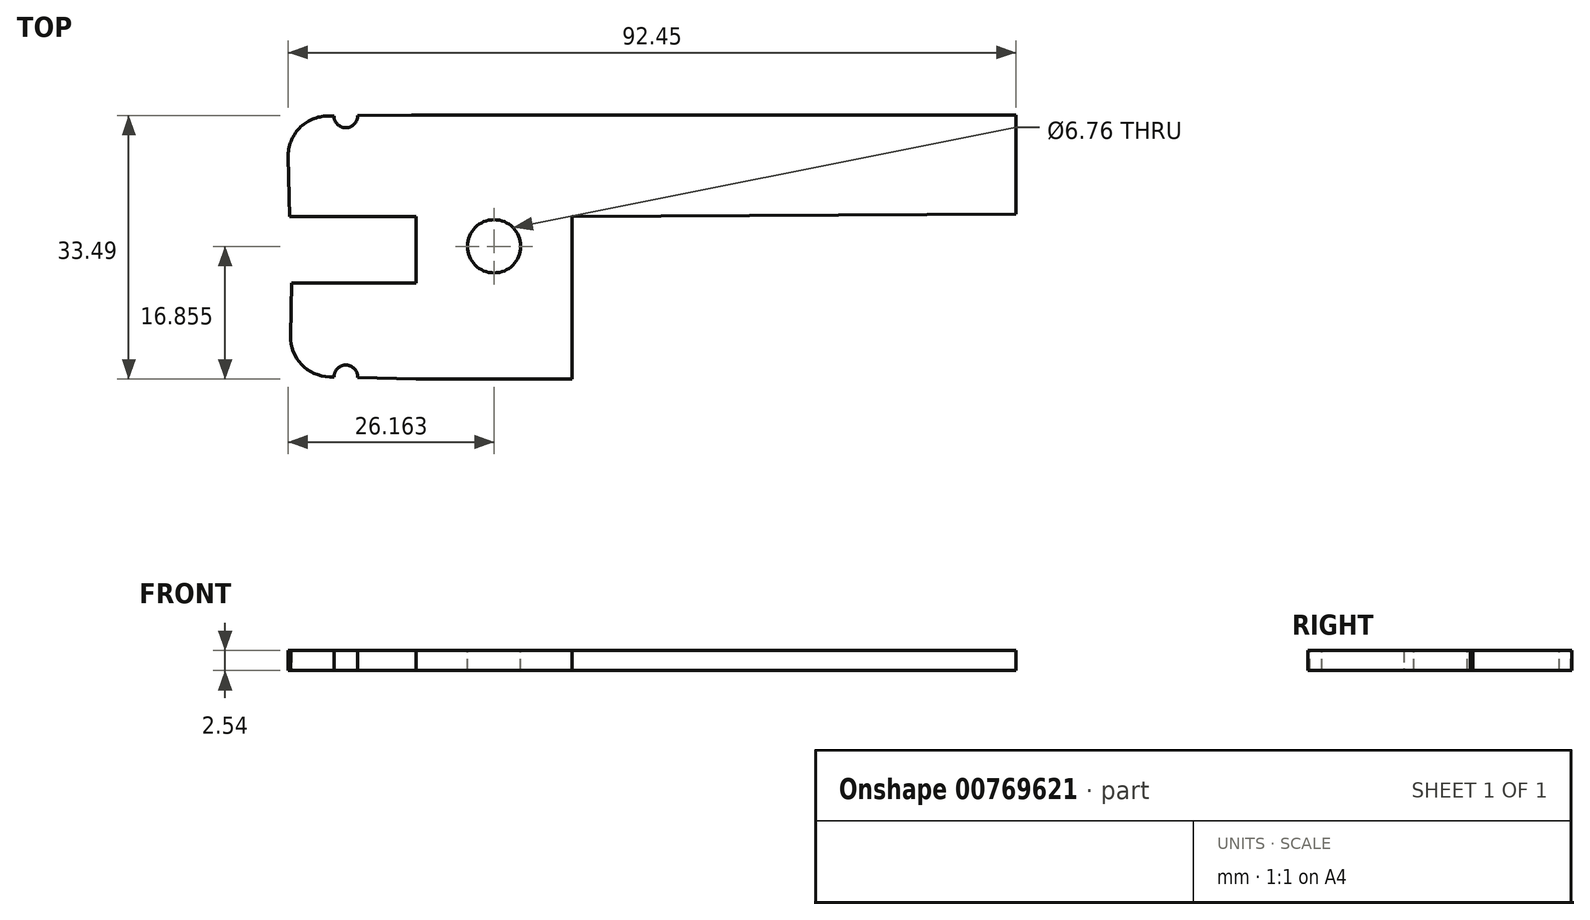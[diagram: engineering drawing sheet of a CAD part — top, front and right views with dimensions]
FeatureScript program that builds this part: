
annotation { "Feature Type Name" : "Feature", "Feature Type Description" : "" }
export const myFeature = defineFeature(function(context is Context, id is Id, definition is map)
    precondition{}
    {
        {
            var Q0;
            Q0=qCreatedBy(makeId("Top.planeOp"),FACE);
            var sketch = newSketch(context, id + "F0", { "sketchPlane" : qUnion([Q0])});
            skLineSegment(sketch, "E0", {"start": v(-46, 24.97) * mm, "end": v(-29.94, 24.97) * mm});
            skLineSegment(sketch, "E1", {"start": v(-29.94, 24.97) * mm, "end": v(-29.94, 16.5) * mm});
            skLineSegment(sketch, "E2", {"start": v(-29.94, 16.5) * mm, "end": v(-45.7, 16.5) * mm});
            skLineSegment(sketch, "E3", {"start": v(-45.7, 16.5) * mm, "end": v(-46, 4.72) * mm});
            skLineSegment(sketch, "E4", {"start": v(-46, 4.72) * mm, "end": v(-29.94, 4.32) * mm});
            skLineSegment(sketch, "E5", {"start": v(-29.94, 4.32) * mm, "end": v(-10.08, 4.32) * mm});
            skLineSegment(sketch, "E6", {"start": v(-10.08, 4.32) * mm, "end": v(-10.08, 24.97) * mm});
            skLineSegment(sketch, "E7", {"start": v(-46.3, 37.68) * mm, "end": v(-46, 24.97) * mm});
            skLineSegment(sketch, "E8", {"start": v(-46.3, 37.68) * mm, "end": v(-30.51, 37.81) * mm});
            skLineSegment(sketch, "E9", {"start": v(-30.51, 37.81) * mm, "end": v(46.28, 37.81) * mm});
            skLineSegment(sketch, "E10", {"start": v(46.28, 37.81) * mm, "end": v(46.28, 25.26) * mm});
            skLineSegment(sketch, "E11", {"start": v(-10.08, 24.97) * mm, "end": v(46.28, 25.26) * mm});
            skSolve(sketch);
        }
        {
            var Q0;
            Q0=makeQuery(id+"F0.imprint","IMPRINT",FACE,{"disambiguationData":[TD([[makeQuery(id+"F0.imprint","IMPRINT",EDGE,{"derivedFrom":sQuery(id+"F0.wireOp",EDGE,"E0")}),1.0]])]});
            extrude(context, id + "F1", {"entities" : qUnion([Q0]), "depth" : 2.54 * mm, "offsetDistance" : 25.4 * mm});
        }
        {
            var Q0;
            Q0=makeQuery(id+"F1.opExtrude","CAP_FACE",FACE,{"disambiguationData":[OSD([sQuery(id+"F0.wireOp",EDGE,"E0"),sQuery(id+"F0.wireOp",EDGE,"E1"),sQuery(id+"F0.wireOp",EDGE,"E2"),sQuery(id+"F0.wireOp",EDGE,"E3"),sQuery(id+"F0.wireOp",EDGE,"E4"),sQuery(id+"F0.wireOp",EDGE,"E5"),sQuery(id+"F0.wireOp",EDGE,"E6"),sQuery(id+"F0.wireOp",EDGE,"E7"),sQuery(id+"F0.wireOp",EDGE,"E8"),sQuery(id+"F0.wireOp",EDGE,"E9"),sQuery(id+"F0.wireOp",EDGE,"E10"),sQuery(id+"F0.wireOp",EDGE,"E11")])],"isStart":false});
            var sketch = newSketch(context, id + "F2", { "sketchPlane" : qUnion([Q0])});
            skPoint(sketch, "E12", {"position": v(-20, 21.17) * mm});
            skPoint(sketch, "E12.positionSnap0", {"position": v(-20, 4.32) * mm});
            skSolve(sketch);
        }
        {
            var Q0;
            Q0=sQuery(id+"F2.wireOp",VERTEX,"E12");
            var Q1;
            Q1=makeQuery(id+"F1.opExtrude","SWEPT_BODY",BODY,{"disambiguationData":[OSD([sQuery(id+"F0.wireOp",EDGE,"E0"),sQuery(id+"F0.wireOp",EDGE,"E1"),sQuery(id+"F0.wireOp",EDGE,"E2"),sQuery(id+"F0.wireOp",EDGE,"E3"),sQuery(id+"F0.wireOp",EDGE,"E4"),sQuery(id+"F0.wireOp",EDGE,"E5"),sQuery(id+"F0.wireOp",EDGE,"E6"),sQuery(id+"F0.wireOp",EDGE,"E7"),sQuery(id+"F0.wireOp",EDGE,"E8"),sQuery(id+"F0.wireOp",EDGE,"E9"),sQuery(id+"F0.wireOp",EDGE,"E10"),sQuery(id+"F0.wireOp",EDGE,"E11")])]});
            hole(context, id + "F3", {"style" : HoleStyle.SIMPLE, "endStyle" : HoleEndStyle.THROUGH, "standardTappedOrClearance" : lookupTablePath({ "standard" : "ANSI", "fit" : "Normal (ASME)", "size" : "1/4", "type" : "Clearance" }), "standardBlindInLast" : lookupTablePath({ "fit" : "Free", "standard" : "ANSI", "size" : "1/4", "type" : "Clearance" }), "holeDiameter" : 6.76 * mm, "majorDiameter" : 6.35 * mm, "isTappedThrough" : true, "tappedDepth" : 12.7 * mm, "tapClearance" : 3, "locations" : qUnion([Q0]), "scope" : qUnion([Q1])});
        }
        {
            var Q0;
            Q0=makeQuery(id+"F1.opExtrude","SWEPT_EDGE",EDGE,{"disambiguationData":[OSD([sQuery(id+"F0.wireOp",EDGE,"E3"),sQuery(id+"F0.wireOp",EDGE,"E4")])]});
            fillet(context, id + "F4", {"entities" : qUnion([Q0]), "radius" : 5.08 * mm, "tangentPropagation" : true, "allowEdgeOverflow" : false});
        }
        {
            var Q0;
            Q0=makeQuery(id+"F1.opExtrude","SWEPT_EDGE",EDGE,{"disambiguationData":[OSD([sQuery(id+"F0.wireOp",EDGE,"E7"),sQuery(id+"F0.wireOp",EDGE,"E8")])]});
            fillet(context, id + "F5", {"entities" : qUnion([Q0]), "radius" : 5.08 * mm, "tangentPropagation" : true, "allowEdgeOverflow" : false});
        }
        {
            var Q0;
            Q0=makeQuery(id+"F1.opExtrude","CAP_FACE",FACE,{"disambiguationData":[OSD([sQuery(id+"F0.wireOp",EDGE,"E0"),sQuery(id+"F0.wireOp",EDGE,"E1"),sQuery(id+"F0.wireOp",EDGE,"E2"),sQuery(id+"F0.wireOp",EDGE,"E3"),sQuery(id+"F0.wireOp",EDGE,"E4"),sQuery(id+"F0.wireOp",EDGE,"E5"),sQuery(id+"F0.wireOp",EDGE,"E6"),sQuery(id+"F0.wireOp",EDGE,"E7"),sQuery(id+"F0.wireOp",EDGE,"E8"),sQuery(id+"F0.wireOp",EDGE,"E9"),sQuery(id+"F0.wireOp",EDGE,"E10"),sQuery(id+"F0.wireOp",EDGE,"E11")])],"isStart":false});
            var sketch = newSketch(context, id + "F6", { "sketchPlane" : qUnion([Q0])});
            skPoint(sketch, "E13", {"position": v(-38.85, 4.54) * mm});
            skPoint(sketch, "E14", {"position": v(-38.85, 37.73) * mm});
            skSolve(sketch);
        }
        {
            var Q0;
            Q0=sQuery(id+"F6.wireOp",VERTEX,"E14");
            var Q1;
            Q1=makeQuery(id+"F1.opExtrude","SWEPT_BODY",BODY,{"disambiguationData":[OSD([sQuery(id+"F0.wireOp",EDGE,"E0"),sQuery(id+"F0.wireOp",EDGE,"E1"),sQuery(id+"F0.wireOp",EDGE,"E2"),sQuery(id+"F0.wireOp",EDGE,"E3"),sQuery(id+"F0.wireOp",EDGE,"E4"),sQuery(id+"F0.wireOp",EDGE,"E5"),sQuery(id+"F0.wireOp",EDGE,"E6"),sQuery(id+"F0.wireOp",EDGE,"E7"),sQuery(id+"F0.wireOp",EDGE,"E8"),sQuery(id+"F0.wireOp",EDGE,"E9"),sQuery(id+"F0.wireOp",EDGE,"E10"),sQuery(id+"F0.wireOp",EDGE,"E11")])]});
            hole(context, id + "F7", {"style" : HoleStyle.SIMPLE, "endStyle" : HoleEndStyle.THROUGH, "holeDiameter" : 3 * mm, "majorDiameter" : 6.35 * mm, "isTappedThrough" : true, "tappedDepth" : 12.7 * mm, "tapClearance" : 3, "locations" : qUnion([Q0]), "scope" : qUnion([Q1])});
        }
        {
            var Q0;
            Q0=makeQuery(id+"F1.opExtrude","CAP_FACE",FACE,{"disambiguationData":[OSD([sQuery(id+"F0.wireOp",EDGE,"E0"),sQuery(id+"F0.wireOp",EDGE,"E1"),sQuery(id+"F0.wireOp",EDGE,"E2"),sQuery(id+"F0.wireOp",EDGE,"E3"),sQuery(id+"F0.wireOp",EDGE,"E4"),sQuery(id+"F0.wireOp",EDGE,"E5"),sQuery(id+"F0.wireOp",EDGE,"E6"),sQuery(id+"F0.wireOp",EDGE,"E7"),sQuery(id+"F0.wireOp",EDGE,"E8"),sQuery(id+"F0.wireOp",EDGE,"E9"),sQuery(id+"F0.wireOp",EDGE,"E10"),sQuery(id+"F0.wireOp",EDGE,"E11")])],"isStart":false});
            var sketch = newSketch(context, id + "F8", { "sketchPlane" : qUnion([Q0])});
            skPoint(sketch, "E15", {"position": v(-38.84, 4.6) * mm});
            skPoint(sketch, "E15.positionSnap0", {"position": v(-38.84, 36.23) * mm});
            skSolve(sketch);
        }
        {
            var Q0;
            Q0=sQuery(id+"F8.wireOp",VERTEX,"E15");
            var Q1;
            Q1=makeQuery(id+"F1.opExtrude","SWEPT_BODY",BODY,{"disambiguationData":[OSD([sQuery(id+"F0.wireOp",EDGE,"E0"),sQuery(id+"F0.wireOp",EDGE,"E1"),sQuery(id+"F0.wireOp",EDGE,"E2"),sQuery(id+"F0.wireOp",EDGE,"E3"),sQuery(id+"F0.wireOp",EDGE,"E4"),sQuery(id+"F0.wireOp",EDGE,"E5"),sQuery(id+"F0.wireOp",EDGE,"E6"),sQuery(id+"F0.wireOp",EDGE,"E7"),sQuery(id+"F0.wireOp",EDGE,"E8"),sQuery(id+"F0.wireOp",EDGE,"E9"),sQuery(id+"F0.wireOp",EDGE,"E10"),sQuery(id+"F0.wireOp",EDGE,"E11")])]});
            hole(context, id + "F9", {"style" : HoleStyle.SIMPLE, "endStyle" : HoleEndStyle.THROUGH, "holeDiameter" : 3 * mm, "majorDiameter" : 6.35 * mm, "isTappedThrough" : true, "tappedDepth" : 12.7 * mm, "tapClearance" : 3, "locations" : qUnion([Q0]), "scope" : qUnion([Q1])});
        }
    });
